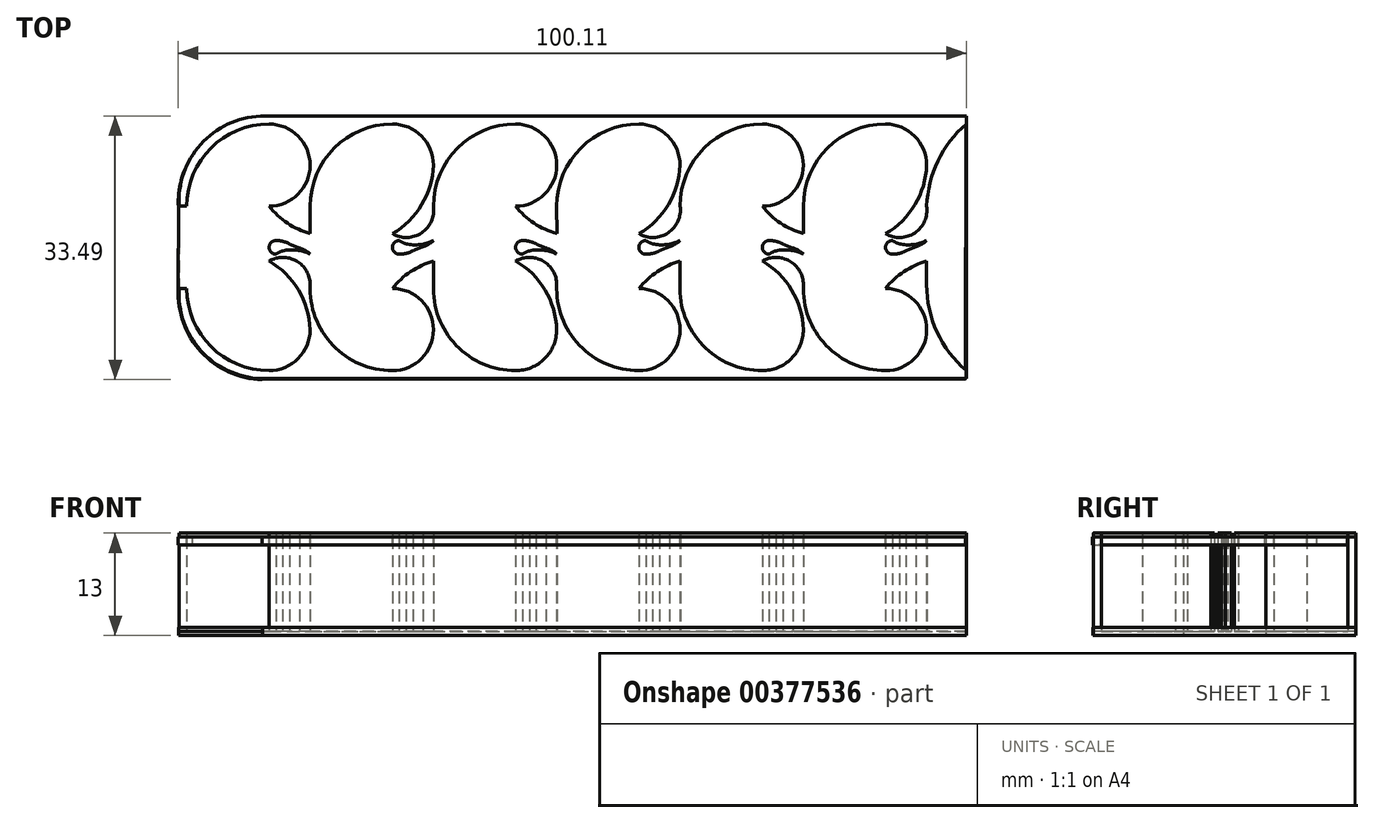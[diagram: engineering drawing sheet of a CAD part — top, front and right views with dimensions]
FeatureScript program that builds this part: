
annotation { "Feature Type Name" : "Feature", "Feature Type Description" : "" }
export const myFeature = defineFeature(function(context is Context, id is Id, definition is map)
    precondition{}
    {
        {
            var Q0;
            Q0=qCreatedBy(makeId("Top.planeOp"),FACE);
            var sketch = newSketch(context, id + "F0", { "sketchPlane" : qUnion([Q0])});
            skPoint(sketch, "E0", {"position": v(94.94, 29.27) * mm});
            skPoint(sketch, "E1", {"position": v(95.94, 28.27) * mm});
            skPoint(sketch, "E2", {"position": v(95.94, -3.06) * mm});
            skPoint(sketch, "E3", {"position": v(94.94, -4.06) * mm});
            skPoint(sketch, "E4", {"position": v(94.94, -3.06) * mm});
            skPoint(sketch, "E5", {"position": v(-3.06, 17.83) * mm});
            skPoint(sketch, "E6", {"position": v(-3.06, 7.38) * mm});
            skLineSegment(sketch, "E7", {"start": v(-3.06, 17.83) * mm, "end": v(-4.06, 17.83) * mm});
            skLineSegment(sketch, "E8", {"start": v(-4.06, 7.38) * mm, "end": v(-3.06, 7.38) * mm});
            skPoint(sketch, "E9", {"position": v(7.38, 28.27) * mm});
            skPoint(sketch, "E10", {"position": v(7.38, -3.06) * mm});
            skArc(sketch, "E11", {"start": v(7.38, 28.27) * mm, "mid": v(0, 25.21) * mm, "end": v(-3.06, 17.83) * mm});
            skArc(sketch, "E12", {"start": v(-3.06, 7.38) * mm, "mid": v(0, 0) * mm, "end": v(7.38, -3.06) * mm});
            skArc(sketch, "E13", {"start": v(7.38, 17.83) * mm, "mid": v(12.6, 23.05) * mm, "end": v(7.38, 28.27) * mm});
            skPoint(sketch, "E14", {"position": v(12.6, 23.05) * mm});
            skPoint(sketch, "E15", {"position": v(0, 25.21) * mm});
            skPoint(sketch, "E16", {"position": v(0, 0) * mm});
            skPoint(sketch, "E17", {"position": v(12.6, 2.16) * mm});
            skPoint(sketch, "E18", {"position": v(-4.06, 12.6) * mm});
            skPoint(sketch, "E19", {"position": v(7.38, 12.6) * mm});
            skPoint(sketch, "E20", {"position": v(7.38, 10.87) * mm});
            skPoint(sketch, "E21", {"position": v(7.38, 14.35) * mm});
            skArc(sketch, "E22", {"start": v(12.6, 2.16) * mm, "mid": v(11.12, 7.2) * mm, "end": v(7.38, 10.87) * mm});
            skArc(sketch, "E23", {"start": v(23.05, 28.27) * mm, "mid": v(15.66, 25.21) * mm, "end": v(12.6, 17.83) * mm});
            skArc(sketch, "E24", {"start": v(12.6, 7.86) * mm, "mid": v(15.49, 0.17) * mm, "end": v(23.03, -3.06) * mm});
            skPoint(sketch, "E25", {"position": v(28.27, 23.05) * mm});
            skPoint(sketch, "E26", {"position": v(15.66, 25.21) * mm});
            skPoint(sketch, "E27", {"position": v(15.49, 0.17) * mm});
            skPoint(sketch, "E28", {"position": v(28.27, 2.16) * mm});
            skPoint(sketch, "E29", {"position": v(23.05, 12.6) * mm});
            skPoint(sketch, "E30", {"position": v(23.05, 14.35) * mm});
            skArc(sketch, "E31", {"start": v(23.05, 14.35) * mm, "mid": v(26.78, 18.02) * mm, "end": v(28.27, 23.05) * mm});
            skPoint(sketch, "E32", {"position": v(11.12, 7.2) * mm});
            skLineSegment(sketch, "E33", {"start": v(12.6, 17.83) * mm, "end": v(12.6, 14.35) * mm});
            skArc(sketch, "E34", {"start": v(12.6, 7.86) * mm, "mid": v(10.86, 10.87) * mm, "end": v(7.38, 10.87) * mm});
            skArc(sketch, "E35", {"start": v(7.38, 17.83) * mm, "mid": v(9.73, 15.69) * mm, "end": v(12.6, 14.35) * mm});
            skPoint(sketch, "E36", {"position": v(12.6, 12.6) * mm});
            skPoint(sketch, "E37", {"position": v(7.38, 13.48) * mm});
            skPoint(sketch, "E38", {"position": v(12.6, 11.74) * mm});
            skPoint(sketch, "E39", {"position": v(12.6, 13.48) * mm});
            skPoint(sketch, "E40", {"position": v(9.12, 12.6) * mm});
            skPoint(sketch, "E41", {"position": v(10.87, 12.6) * mm});
            skLineSegment(sketch, "E42", {"start": v(7.38, 12.6) * mm, "end": v(9.12, 12.6) * mm});
            skLineSegment(sketch, "E43", {"start": v(9.12, 12.6) * mm, "end": v(10.87, 12.6) * mm});
            skPoint(sketch, "E44", {"position": v(8.25, 12.6) * mm});
            skPoint(sketch, "E45", {"position": v(10, 12.6) * mm});
            skPoint(sketch, "E46", {"position": v(11.74, 12.6) * mm});
            skArc(sketch, "E47", {"start": v(8.25, 13.48) * mm, "mid": v(7.38, 12.6) * mm, "end": v(8.25, 11.74) * mm});
            skArc(sketch, "E48", {"start": v(10, 13.04) * mm, "mid": v(9.15, 13.37) * mm, "end": v(8.25, 13.48) * mm});
            skPoint(sketch, "E49", {"position": v(12.6, 12.17) * mm});
            skPoint(sketch, "E50", {"position": v(12.6, 13.04) * mm});
            skPoint(sketch, "E51", {"position": v(10, 12.17) * mm});
            skArc(sketch, "E52", {"start": v(9.12, 12.17) * mm, "mid": v(8.67, 11.99) * mm, "end": v(8.25, 11.74) * mm});
            skPoint(sketch, "E53.endSnap0", {"position": v(8.25, 13.04) * mm});
            skPoint(sketch, "E54", {"position": v(11.27, 12.52) * mm});
            skPoint(sketch, "E55", {"position": v(11.27, 12.7) * mm});
            skArc(sketch, "E56", {"start": v(12.6, 11.74) * mm, "mid": v(11.98, 12.2) * mm, "end": v(11.27, 12.52) * mm});
            skArc(sketch, "E57", {"start": v(10, 13.04) * mm, "mid": v(10.62, 12.76) * mm, "end": v(11.27, 12.52) * mm});
            skArc(sketch, "E58", {"start": v(12.6, 11.74) * mm, "mid": v(10.9, 12.26) * mm, "end": v(9.12, 12.17) * mm});
            skArc(sketch, "E59", {"start": v(23.05, -3.06) * mm, "mid": v(28.27, 2.16) * mm, "end": v(23.05, 7.38) * mm});
            skArc(sketch, "E60", {"start": v(38.7, 28.27) * mm, "mid": v(31.33, 25.21) * mm, "end": v(28.27, 17.83) * mm});
            skArc(sketch, "E61", {"start": v(28.27, 7.86) * mm, "mid": v(31.15, 0.17) * mm, "end": v(38.7, -3.06) * mm});
            skArc(sketch, "E62", {"start": v(38.7, 17.83) * mm, "mid": v(43.93, 23.05) * mm, "end": v(38.7, 28.27) * mm});
            skPoint(sketch, "E63", {"position": v(43.93, 23.05) * mm});
            skPoint(sketch, "E64", {"position": v(31.33, 25.21) * mm});
            skPoint(sketch, "E65", {"position": v(31.15, 0.17) * mm});
            skPoint(sketch, "E66", {"position": v(43.93, 2.16) * mm});
            skPoint(sketch, "E67", {"position": v(38.7, 12.6) * mm});
            skPoint(sketch, "E68", {"position": v(38.7, 10.87) * mm});
            skPoint(sketch, "E69", {"position": v(38.7, 14.35) * mm});
            skArc(sketch, "E70", {"start": v(43.93, 2.16) * mm, "mid": v(42.45, 7.2) * mm, "end": v(38.7, 10.87) * mm});
            skArc(sketch, "E71", {"start": v(23.05, 14.35) * mm, "mid": v(26.76, 14.44) * mm, "end": v(28.27, 17.83) * mm});
            skPoint(sketch, "E72", {"position": v(26.78, 7.2) * mm});
            skArc(sketch, "E73", {"start": v(28.27, 10.87) * mm, "mid": v(25.39, 9.53) * mm, "end": v(23.05, 7.38) * mm});
            skLineSegment(sketch, "E74", {"start": v(28.27, 7.86) * mm, "end": v(28.27, 10.87) * mm});
            skPoint(sketch, "E75", {"position": v(28.27, 12.6) * mm});
            skPoint(sketch, "E76", {"position": v(23.05, 13.48) * mm});
            skPoint(sketch, "E77", {"position": v(28.27, 11.74) * mm});
            skPoint(sketch, "E78", {"position": v(28.27, 13.48) * mm});
            skPoint(sketch, "E79", {"position": v(24.79, 12.6) * mm});
            skPoint(sketch, "E80", {"position": v(26.53, 12.6) * mm});
            skLineSegment(sketch, "E81", {"start": v(23.05, 12.6) * mm, "end": v(24.79, 12.6) * mm});
            skLineSegment(sketch, "E82", {"start": v(24.79, 12.6) * mm, "end": v(26.53, 12.6) * mm});
            skPoint(sketch, "E83", {"position": v(23.92, 12.6) * mm});
            skPoint(sketch, "E84", {"position": v(25.66, 12.6) * mm});
            skPoint(sketch, "E85", {"position": v(27.4, 12.6) * mm});
            skArc(sketch, "E86", {"start": v(23.92, 13.48) * mm, "mid": v(23.05, 12.6) * mm, "end": v(23.92, 11.74) * mm});
            skPoint(sketch, "E87", {"position": v(28.27, 12.17) * mm});
            skPoint(sketch, "E88", {"position": v(28.27, 13.04) * mm});
            skPoint(sketch, "E89", {"position": v(25.66, 12.17) * mm});
            skArc(sketch, "E90", {"start": v(23.92, 13.48) * mm, "mid": v(24.34, 13.23) * mm, "end": v(24.79, 13.04) * mm});
            skPoint(sketch, "E90.endSnap0", {"position": v(23.92, 13.04) * mm});
            skArc(sketch, "E91", {"start": v(23.92, 11.74) * mm, "mid": v(24.82, 11.84) * mm, "end": v(25.66, 12.17) * mm});
            skPoint(sketch, "E92", {"position": v(26.93, 12.52) * mm});
            skPoint(sketch, "E93", {"position": v(26.93, 12.7) * mm});
            skArc(sketch, "E94", {"start": v(26.93, 12.7) * mm, "mid": v(26.29, 12.45) * mm, "end": v(25.66, 12.17) * mm});
            skArc(sketch, "E95", {"start": v(26.93, 12.7) * mm, "mid": v(27.65, 13.01) * mm, "end": v(28.27, 13.48) * mm});
            skArc(sketch, "E96", {"start": v(24.79, 13.04) * mm, "mid": v(26.57, 12.96) * mm, "end": v(28.27, 13.48) * mm});
            skArc(sketch, "E97", {"start": v(54.37, 28.27) * mm, "mid": v(46.99, 25.21) * mm, "end": v(43.93, 17.83) * mm});
            skArc(sketch, "E98", {"start": v(43.93, 7.86) * mm, "mid": v(46.81, 0.17) * mm, "end": v(54.36, -3.06) * mm});
            skPoint(sketch, "E99", {"position": v(59.6, 23.05) * mm});
            skPoint(sketch, "E100", {"position": v(46.99, 25.21) * mm});
            skPoint(sketch, "E101", {"position": v(46.81, 0.17) * mm});
            skPoint(sketch, "E102", {"position": v(59.6, 2.16) * mm});
            skPoint(sketch, "E103", {"position": v(54.37, 12.6) * mm});
            skPoint(sketch, "E104", {"position": v(54.37, 14.35) * mm});
            skArc(sketch, "E105", {"start": v(54.37, 14.35) * mm, "mid": v(58.1, 18.02) * mm, "end": v(59.6, 23.05) * mm});
            skPoint(sketch, "E106", {"position": v(42.45, 7.2) * mm});
            skLineSegment(sketch, "E107", {"start": v(43.93, 17.83) * mm, "end": v(43.93, 14.35) * mm});
            skArc(sketch, "E108", {"start": v(43.93, 7.86) * mm, "mid": v(42.19, 10.87) * mm, "end": v(38.7, 10.87) * mm});
            skArc(sketch, "E109", {"start": v(38.7, 17.83) * mm, "mid": v(41.05, 15.69) * mm, "end": v(43.93, 14.35) * mm});
            skPoint(sketch, "E110", {"position": v(43.93, 12.6) * mm});
            skPoint(sketch, "E111", {"position": v(38.7, 13.48) * mm});
            skPoint(sketch, "E112", {"position": v(38.7, 11.74) * mm});
            skPoint(sketch, "E113", {"position": v(43.93, 11.74) * mm});
            skPoint(sketch, "E114", {"position": v(43.93, 13.48) * mm});
            skPoint(sketch, "E115", {"position": v(40.45, 12.6) * mm});
            skPoint(sketch, "E116", {"position": v(42.2, 12.6) * mm});
            skLineSegment(sketch, "E117", {"start": v(38.7, 12.6) * mm, "end": v(40.45, 12.6) * mm});
            skLineSegment(sketch, "E118", {"start": v(40.45, 12.6) * mm, "end": v(42.2, 12.6) * mm});
            skPoint(sketch, "E119", {"position": v(39.58, 12.6) * mm});
            skPoint(sketch, "E120", {"position": v(41.32, 12.6) * mm});
            skPoint(sketch, "E121", {"position": v(43.06, 12.6) * mm});
            skArc(sketch, "E122", {"start": v(39.58, 13.48) * mm, "mid": v(38.7, 12.6) * mm, "end": v(39.58, 11.74) * mm});
            skArc(sketch, "E123", {"start": v(41.32, 13.04) * mm, "mid": v(40.48, 13.37) * mm, "end": v(39.58, 13.48) * mm});
            skPoint(sketch, "E124", {"position": v(43.93, 12.17) * mm});
            skPoint(sketch, "E125", {"position": v(43.93, 13.04) * mm});
            skPoint(sketch, "E126", {"position": v(41.32, 12.17) * mm});
            skArc(sketch, "E127", {"start": v(40.45, 12.17) * mm, "mid": v(40, 11.99) * mm, "end": v(39.58, 11.74) * mm});
            skPoint(sketch, "E128.endSnap0", {"position": v(39.58, 13.04) * mm});
            skPoint(sketch, "E129", {"position": v(42.6, 12.52) * mm});
            skPoint(sketch, "E130", {"position": v(42.6, 12.7) * mm});
            skArc(sketch, "E131", {"start": v(43.93, 11.74) * mm, "mid": v(43.3, 12.2) * mm, "end": v(42.6, 12.52) * mm});
            skArc(sketch, "E132", {"start": v(41.32, 13.04) * mm, "mid": v(41.95, 12.76) * mm, "end": v(42.6, 12.52) * mm});
            skArc(sketch, "E133", {"start": v(43.93, 11.74) * mm, "mid": v(42.23, 12.26) * mm, "end": v(40.45, 12.17) * mm});
            skArc(sketch, "E134", {"start": v(54.37, -3.06) * mm, "mid": v(59.6, 2.16) * mm, "end": v(54.37, 7.38) * mm});
            skArc(sketch, "E135", {"start": v(70.03, 28.27) * mm, "mid": v(62.65, 25.21) * mm, "end": v(59.6, 17.83) * mm});
            skArc(sketch, "E136", {"start": v(59.6, 7.86) * mm, "mid": v(62.48, 0.17) * mm, "end": v(70.02, -3.06) * mm});
            skArc(sketch, "E137", {"start": v(70.03, 17.83) * mm, "mid": v(75.25, 23.05) * mm, "end": v(70.03, 28.27) * mm});
            skPoint(sketch, "E138", {"position": v(75.25, 23.05) * mm});
            skPoint(sketch, "E139", {"position": v(62.65, 25.21) * mm});
            skPoint(sketch, "E140", {"position": v(62.48, 0.17) * mm});
            skPoint(sketch, "E141", {"position": v(75.25, 2.16) * mm});
            skPoint(sketch, "E142", {"position": v(70.03, 12.6) * mm});
            skPoint(sketch, "E143", {"position": v(70.03, 10.87) * mm});
            skArc(sketch, "E144", {"start": v(75.25, 2.16) * mm, "mid": v(73.77, 7.2) * mm, "end": v(70.03, 10.87) * mm});
            skArc(sketch, "E145", {"start": v(54.37, 14.35) * mm, "mid": v(58.08, 14.44) * mm, "end": v(59.6, 17.83) * mm});
            skPoint(sketch, "E146", {"position": v(58.1, 7.2) * mm});
            skArc(sketch, "E147", {"start": v(59.6, 10.87) * mm, "mid": v(56.71, 9.53) * mm, "end": v(54.37, 7.38) * mm});
            skLineSegment(sketch, "E148", {"start": v(59.6, 7.86) * mm, "end": v(59.6, 10.87) * mm});
            skPoint(sketch, "E149", {"position": v(59.6, 12.6) * mm});
            skPoint(sketch, "E150", {"position": v(54.37, 13.48) * mm});
            skPoint(sketch, "E151", {"position": v(59.6, 11.74) * mm});
            skPoint(sketch, "E152", {"position": v(59.6, 13.48) * mm});
            skPoint(sketch, "E153", {"position": v(56.11, 12.6) * mm});
            skPoint(sketch, "E154", {"position": v(57.85, 12.6) * mm});
            skLineSegment(sketch, "E155", {"start": v(54.37, 12.6) * mm, "end": v(56.11, 12.6) * mm});
            skLineSegment(sketch, "E156", {"start": v(56.11, 12.6) * mm, "end": v(57.85, 12.6) * mm});
            skPoint(sketch, "E157", {"position": v(55.24, 12.6) * mm});
            skPoint(sketch, "E158", {"position": v(56.98, 12.6) * mm});
            skPoint(sketch, "E159", {"position": v(58.72, 12.6) * mm});
            skArc(sketch, "E160", {"start": v(55.24, 13.48) * mm, "mid": v(54.37, 12.6) * mm, "end": v(55.24, 11.74) * mm});
            skPoint(sketch, "E161", {"position": v(59.6, 12.17) * mm});
            skPoint(sketch, "E162", {"position": v(59.6, 13.04) * mm});
            skPoint(sketch, "E163", {"position": v(56.98, 12.17) * mm});
            skArc(sketch, "E164", {"start": v(55.24, 13.48) * mm, "mid": v(55.66, 13.23) * mm, "end": v(56.11, 13.04) * mm});
            skPoint(sketch, "E164.endSnap0", {"position": v(55.24, 13.04) * mm});
            skArc(sketch, "E165", {"start": v(55.24, 11.74) * mm, "mid": v(56.14, 11.84) * mm, "end": v(56.98, 12.17) * mm});
            skPoint(sketch, "E166", {"position": v(58.26, 12.7) * mm});
            skArc(sketch, "E167", {"start": v(58.26, 12.7) * mm, "mid": v(57.61, 12.45) * mm, "end": v(56.98, 12.17) * mm});
            skArc(sketch, "E168", {"start": v(58.26, 12.7) * mm, "mid": v(58.97, 13.01) * mm, "end": v(59.6, 13.48) * mm});
            skArc(sketch, "E169", {"start": v(56.11, 13.04) * mm, "mid": v(57.9, 12.96) * mm, "end": v(59.6, 13.48) * mm});
            skPoint(sketch, "E170", {"position": v(70.03, 14.35) * mm});
            skArc(sketch, "E171", {"start": v(85.7, 28.27) * mm, "mid": v(78.31, 25.21) * mm, "end": v(75.26, 17.83) * mm});
            skArc(sketch, "E172", {"start": v(75.26, 7.86) * mm, "mid": v(78.14, 0.17) * mm, "end": v(85.69, -3.06) * mm});
            skPoint(sketch, "E173", {"position": v(90.92, 23.05) * mm});
            skPoint(sketch, "E174", {"position": v(78.31, 25.21) * mm});
            skPoint(sketch, "E175", {"position": v(78.14, 0.17) * mm});
            skPoint(sketch, "E176", {"position": v(90.92, 2.16) * mm});
            skPoint(sketch, "E177", {"position": v(85.7, 12.6) * mm});
            skPoint(sketch, "E178", {"position": v(85.7, 10.87) * mm});
            skPoint(sketch, "E179", {"position": v(85.7, 14.35) * mm});
            skArc(sketch, "E180", {"start": v(85.7, 14.35) * mm, "mid": v(89.43, 18.02) * mm, "end": v(90.92, 23.05) * mm});
            skPoint(sketch, "E181", {"position": v(73.77, 7.2) * mm});
            skLineSegment(sketch, "E182", {"start": v(75.26, 17.83) * mm, "end": v(75.26, 14.35) * mm});
            skArc(sketch, "E183", {"start": v(75.26, 7.86) * mm, "mid": v(73.52, 10.87) * mm, "end": v(70.03, 10.87) * mm});
            skArc(sketch, "E184", {"start": v(70.03, 17.83) * mm, "mid": v(72.38, 15.69) * mm, "end": v(75.26, 14.35) * mm});
            skPoint(sketch, "E185", {"position": v(75.26, 12.6) * mm});
            skPoint(sketch, "E186", {"position": v(75.26, 11.74) * mm});
            skPoint(sketch, "E187", {"position": v(75.26, 13.48) * mm});
            skPoint(sketch, "E188", {"position": v(71.77, 12.6) * mm});
            skPoint(sketch, "E189", {"position": v(73.52, 12.6) * mm});
            skLineSegment(sketch, "E190", {"start": v(70.03, 12.6) * mm, "end": v(71.77, 12.6) * mm});
            skLineSegment(sketch, "E191", {"start": v(71.77, 12.6) * mm, "end": v(73.52, 12.6) * mm});
            skPoint(sketch, "E192", {"position": v(70.9, 12.6) * mm});
            skPoint(sketch, "E193", {"position": v(72.65, 12.6) * mm});
            skPoint(sketch, "E194", {"position": v(74.39, 12.6) * mm});
            skArc(sketch, "E195", {"start": v(70.9, 13.48) * mm, "mid": v(70.03, 12.6) * mm, "end": v(70.9, 11.74) * mm});
            skArc(sketch, "E196", {"start": v(72.65, 13.04) * mm, "mid": v(71.8, 13.37) * mm, "end": v(70.9, 13.48) * mm});
            skPoint(sketch, "E197", {"position": v(75.26, 12.17) * mm});
            skPoint(sketch, "E198", {"position": v(75.26, 13.04) * mm});
            skPoint(sketch, "E199", {"position": v(72.65, 12.17) * mm});
            skArc(sketch, "E200", {"start": v(71.77, 12.17) * mm, "mid": v(71.32, 11.99) * mm, "end": v(70.9, 11.74) * mm});
            skPoint(sketch, "E201.endSnap0", {"position": v(70.9, 13.04) * mm});
            skPoint(sketch, "E202", {"position": v(73.92, 12.52) * mm});
            skPoint(sketch, "E203", {"position": v(73.92, 12.7) * mm});
            skArc(sketch, "E204", {"start": v(75.26, 11.74) * mm, "mid": v(74.63, 12.2) * mm, "end": v(73.92, 12.52) * mm});
            skArc(sketch, "E205", {"start": v(72.65, 13.04) * mm, "mid": v(73.27, 12.76) * mm, "end": v(73.92, 12.52) * mm});
            skArc(sketch, "E206", {"start": v(75.26, 11.74) * mm, "mid": v(73.55, 12.26) * mm, "end": v(71.77, 12.17) * mm});
            skArc(sketch, "E207", {"start": v(85.7, -3.06) * mm, "mid": v(90.92, 2.16) * mm, "end": v(85.7, 7.38) * mm});
            skPoint(sketch, "E208", {"position": v(93.98, 25.21) * mm});
            skPoint(sketch, "E209", {"position": v(93.8, 0.17) * mm});
            skArc(sketch, "E210", {"start": v(85.7, 14.35) * mm, "mid": v(89.4, 14.44) * mm, "end": v(90.92, 17.83) * mm});
            skPoint(sketch, "E211", {"position": v(89.43, 7.2) * mm});
            skArc(sketch, "E212", {"start": v(90.92, 10.87) * mm, "mid": v(88.04, 9.53) * mm, "end": v(85.7, 7.38) * mm});
            skLineSegment(sketch, "E213", {"start": v(90.92, 7.86) * mm, "end": v(90.92, 10.87) * mm});
            skPoint(sketch, "E214", {"position": v(90.92, 12.6) * mm});
            skPoint(sketch, "E215", {"position": v(90.92, 11.74) * mm});
            skPoint(sketch, "E216", {"position": v(90.92, 13.48) * mm});
            skPoint(sketch, "E217", {"position": v(87.44, 12.6) * mm});
            skPoint(sketch, "E218", {"position": v(89.18, 12.6) * mm});
            skLineSegment(sketch, "E219", {"start": v(85.7, 12.6) * mm, "end": v(87.44, 12.6) * mm});
            skLineSegment(sketch, "E220", {"start": v(87.44, 12.6) * mm, "end": v(89.18, 12.6) * mm});
            skPoint(sketch, "E221", {"position": v(86.57, 12.6) * mm});
            skPoint(sketch, "E222", {"position": v(88.3, 12.6) * mm});
            skPoint(sketch, "E223", {"position": v(90.05, 12.6) * mm});
            skArc(sketch, "E224", {"start": v(86.57, 13.48) * mm, "mid": v(85.7, 12.6) * mm, "end": v(86.57, 11.74) * mm});
            skPoint(sketch, "E225", {"position": v(90.92, 12.17) * mm});
            skPoint(sketch, "E226", {"position": v(90.92, 13.04) * mm});
            skPoint(sketch, "E227", {"position": v(88.3, 12.17) * mm});
            skArc(sketch, "E228", {"start": v(86.57, 13.48) * mm, "mid": v(86.99, 13.23) * mm, "end": v(87.44, 13.04) * mm});
            skPoint(sketch, "E228.endSnap0", {"position": v(86.57, 13.04) * mm});
            skArc(sketch, "E229", {"start": v(86.57, 11.74) * mm, "mid": v(87.47, 11.84) * mm, "end": v(88.3, 12.17) * mm});
            skPoint(sketch, "E230", {"position": v(89.58, 12.52) * mm});
            skPoint(sketch, "E231", {"position": v(89.58, 12.7) * mm});
            skArc(sketch, "E232", {"start": v(89.58, 12.7) * mm, "mid": v(88.94, 12.45) * mm, "end": v(88.3, 12.17) * mm});
            skArc(sketch, "E233", {"start": v(89.58, 12.7) * mm, "mid": v(90.3, 13.01) * mm, "end": v(90.92, 13.48) * mm});
            skArc(sketch, "E234", {"start": v(87.44, 13.04) * mm, "mid": v(89.22, 12.96) * mm, "end": v(90.92, 13.48) * mm});
            skArc(sketch, "E235", {"start": v(23.05, -3.06) * mm, "mid": v(26.74, -1.53) * mm, "end": v(28.27, 2.16) * mm});
            skArc(sketch, "E236", {"start": v(7.38, -3.06) * mm, "mid": v(11.07, -1.53) * mm, "end": v(12.6, 2.16) * mm});
            skArc(sketch, "E237", {"start": v(28.27, 23.05) * mm, "mid": v(26.74, 26.74) * mm, "end": v(23.05, 28.27) * mm});
            skArc(sketch, "E238", {"start": v(38.7, -3.06) * mm, "mid": v(42.4, -1.53) * mm, "end": v(43.93, 2.16) * mm});
            skArc(sketch, "E239", {"start": v(70.02, -3.06) * mm, "mid": v(73.72, -1.53) * mm, "end": v(75.25, 2.16) * mm});
            skArc(sketch, "E240", {"start": v(59.6, 23.05) * mm, "mid": v(58.06, 26.74) * mm, "end": v(54.37, 28.27) * mm});
            skArc(sketch, "E241", {"start": v(90.92, 23.05) * mm, "mid": v(89.39, 26.74) * mm, "end": v(85.7, 28.27) * mm});
            skArc(sketch, "E242", {"start": v(90.92, 7.86) * mm, "mid": v(92.24, 1.85) * mm, "end": v(95.94, -3.06) * mm});
            skArc(sketch, "E243", {"start": v(95.94, 28.27) * mm, "mid": v(92.34, 23.58) * mm, "end": v(90.92, 17.83) * mm});
            skPoint(sketch, "E244", {"position": v(7.38, 29.27) * mm});
            skPoint(sketch, "E245", {"position": v(7.38, -4.06) * mm});
            skPoint(sketch, "E246", {"position": v(-4.06, 6.38) * mm});
            skPoint(sketch, "E247", {"position": v(-4.06, 18.83) * mm});
            skArc(sketch, "E248", {"start": v(-4.06, 6.38) * mm, "mid": v(-0.53, -1.24) * mm, "end": v(7.38, -4.06) * mm});
            skArc(sketch, "E249", {"start": v(7.38, 29.27) * mm, "mid": v(-0.53, 26.46) * mm, "end": v(-4.06, 18.83) * mm});
            skLineSegment(sketch, "E250", {"start": v(7.38, 29.27) * mm, "end": v(95.94, 29.27) * mm});
            skLineSegment(sketch, "E251", {"start": v(95.94, 29.27) * mm, "end": v(95.94, 28.27) * mm});
            skLineSegment(sketch, "E252", {"start": v(95.94, -3.06) * mm, "end": v(95.94, -4.06) * mm});
            skLineSegment(sketch, "E253", {"start": v(95.94, -4.06) * mm, "end": v(7.38, -4.06) * mm});
            skLineSegment(sketch, "E254", {"start": v(-4.06, 6.38) * mm, "end": v(-4.06, 7.38) * mm});
            skLineSegment(sketch, "E255", {"start": v(-3.06, 7.38) * mm, "end": v(-4.06, 7.38) * mm});
            skLineSegment(sketch, "E256", {"start": v(-4.06, 17.83) * mm, "end": v(-3.06, 17.83) * mm});
            skLineSegment(sketch, "E257", {"start": v(-4.06, 17.83) * mm, "end": v(-4.06, 18.83) * mm});
            skPoint(sketch, "E258", {"position": v(11.07, -1.53) * mm});
            skPoint(sketch, "E259", {"position": v(26.74, -1.53) * mm});
            skPoint(sketch, "E260", {"position": v(42.4, -1.53) * mm});
            skPoint(sketch, "E261", {"position": v(73.72, -1.53) * mm});
            skPoint(sketch, "E262", {"position": v(10.86, 10.87) * mm});
            skPoint(sketch, "E263", {"position": v(25.39, 9.53) * mm});
            skPoint(sketch, "E264", {"position": v(42.19, 10.87) * mm});
            skPoint(sketch, "E265", {"position": v(56.71, 9.53) * mm});
            skPoint(sketch, "E266", {"position": v(73.52, 10.87) * mm});
            skPoint(sketch, "E267", {"position": v(88.04, 9.53) * mm});
            skArc(sketch, "E268", {"start": v(12.6, 7.86) * mm, "mid": v(15.5, 0.17) * mm, "end": v(23.05, -3.06) * mm});
            skArc(sketch, "E269", {"start": v(28.27, 2.16) * mm, "mid": v(26.74, 5.85) * mm, "end": v(23.05, 7.38) * mm});
            skLineSegment(sketch, "E270", {"start": v(28.27, 10.87) * mm, "end": v(28.27, 7.86) * mm});
            skArc(sketch, "E271", {"start": v(43.93, 7.86) * mm, "mid": v(46.82, 0.17) * mm, "end": v(54.37, -3.06) * mm});
            skLineSegment(sketch, "E272", {"start": v(59.6, 10.87) * mm, "end": v(59.6, 7.86) * mm});
            skArc(sketch, "E273", {"start": v(75.26, 7.86) * mm, "mid": v(78.14, 0.17) * mm, "end": v(85.7, -3.06) * mm});
            skSolve(sketch);
        }
        {
            var Q0;
            Q0=makeQuery(id+"F0.imprint","IMPRINT",FACE,{"disambiguationData":[TD([[makeQuery(id+"F0.imprint","IMPRINT",EDGE,{"derivedFrom":sQuery(id+"F0.wireOp",EDGE,"E11")}),-1.0]])]});
            var Q1;
            {var subQ8=sQuery(id+"F0.wireOp",EDGE,"E207");Q1=makeQuery(id+"F0.imprint","IMPRINT",FACE,{"disambiguationData":[TD([[makeQuery(id+"F0.imprint","IMPRINT",EDGE,{"derivedFrom":subQ8}),-1.0]])]});}
            var Q2;
            {var subQ1=sQuery(id+"F0.wireOp",EDGE,"E48");Q2=makeQuery(id+"F0.imprint","IMPRINT",FACE,{"disambiguationData":[TD([[makeQuery(id+"F0.imprint","IMPRINT",EDGE,{"derivedFrom":subQ1}),1.0]])]});}
            var Q3;
            {var subQ1=sQuery(id+"F0.wireOp",EDGE,"E90");Q3=makeQuery(id+"F0.imprint","IMPRINT",FACE,{"disambiguationData":[TD([[makeQuery(id+"F0.imprint","IMPRINT",EDGE,{"derivedFrom":subQ1}),-1.0]])]});}
            var Q4;
            {var subQ1=sQuery(id+"F0.wireOp",EDGE,"E123");Q4=makeQuery(id+"F0.imprint","IMPRINT",FACE,{"disambiguationData":[TD([[makeQuery(id+"F0.imprint","IMPRINT",EDGE,{"derivedFrom":subQ1}),1.0]])]});}
            var Q5;
            {var subQ1=sQuery(id+"F0.wireOp",EDGE,"E164");Q5=makeQuery(id+"F0.imprint","IMPRINT",FACE,{"disambiguationData":[TD([[makeQuery(id+"F0.imprint","IMPRINT",EDGE,{"derivedFrom":subQ1}),-1.0]])]});}
            var Q6;
            {var subQ1=sQuery(id+"F0.wireOp",EDGE,"E196");Q6=makeQuery(id+"F0.imprint","IMPRINT",FACE,{"disambiguationData":[TD([[makeQuery(id+"F0.imprint","IMPRINT",EDGE,{"derivedFrom":subQ1}),1.0]])]});}
            var Q7;
            {var subQ1=sQuery(id+"F0.wireOp",EDGE,"E228");Q7=makeQuery(id+"F0.imprint","IMPRINT",FACE,{"disambiguationData":[TD([[makeQuery(id+"F0.imprint","IMPRINT",EDGE,{"derivedFrom":subQ1}),-1.0]])]});}
            extrude(context, id + "F1", {"entities" : qUnion([Q0, Q1, Q2, Q3, Q4, Q5, Q6, Q7]), "depth" : 12 * mm});
        }
        {
            var Q0;
            Q0=qCreatedBy(makeId("Top.planeOp"),FACE);
            var sketch = newSketch(context, id + "F2", { "sketchPlane" : qUnion([Q0])});
            skPoint(sketch, "E274", {"position": v(-4.05, 17.83) * mm});
            skPoint(sketch, "E275", {"position": v(-4.06, 7.39) * mm});
            skPoint(sketch, "E276", {"position": v(6.57, 29.28) * mm});
            skPoint(sketch, "E277", {"position": v(6.57, -4.11) * mm});
            skPoint(sketch, "E278", {"position": v(95.96, 29.28) * mm});
            skPoint(sketch, "E279", {"position": v(95.95, -4.06) * mm});
            skLineSegment(sketch, "E280", {"start": v(6.57, 29.28) * mm, "end": v(95.96, 29.28) * mm});
            skLineSegment(sketch, "E281", {"start": v(95.95, -4.06) * mm, "end": v(95.96, 29.28) * mm});
            skLineSegment(sketch, "E282", {"start": v(95.95, -4.06) * mm, "end": v(6.57, -4.11) * mm});
            skLineSegment(sketch, "E283", {"start": v(-4.05, 17.83) * mm, "end": v(-4.06, 7.39) * mm});
            skArc(sketch, "E284", {"start": v(6.57, 29.28) * mm, "mid": v(-1.17, 25.8) * mm, "end": v(-4.05, 17.83) * mm});
            skArc(sketch, "E285", {"start": v(-4.06, 7.39) * mm, "mid": v(-1.16, -0.6) * mm, "end": v(6.57, -4.11) * mm});
            skSolve(sketch);
        }
        {
            var Q0;
            Q0=makeQuery(id+"F2.imprint","IMPRINT",FACE,{"disambiguationData":[TD([[makeQuery(id+"F2.imprint","IMPRINT",EDGE,{"derivedFrom":sQuery(id+"F2.wireOp",EDGE,"E280")}),-1.0]])]});
            extrude(context, id + "F3", {"entities" : qUnion([Q0]), "endBound" : BoundingType.SYMMETRIC, "depth" : 1 * mm});
        }
        {
            var Q0;
            Q0=makeQuery(id+"F1.opExtrude","CAP_FACE",FACE,{"disambiguationData":[OSD([sQuery(id+"F0.wireOp",EDGE,"E11"),sQuery(id+"F0.wireOp",EDGE,"E13"),sQuery(id+"F0.wireOp",EDGE,"E23"),sQuery(id+"F0.wireOp",EDGE,"E33"),sQuery(id+"F0.wireOp",EDGE,"E35"),sQuery(id+"F0.wireOp",EDGE,"E31"),sQuery(id+"F0.wireOp",EDGE,"E60"),sQuery(id+"F0.wireOp",EDGE,"E71"),sQuery(id+"F0.wireOp",EDGE,"E62"),sQuery(id+"F0.wireOp",EDGE,"E97"),sQuery(id+"F0.wireOp",EDGE,"E107"),sQuery(id+"F0.wireOp",EDGE,"E109"),sQuery(id+"F0.wireOp",EDGE,"E105"),sQuery(id+"F0.wireOp",EDGE,"E135"),sQuery(id+"F0.wireOp",EDGE,"E145"),sQuery(id+"F0.wireOp",EDGE,"E137"),sQuery(id+"F0.wireOp",EDGE,"E171"),sQuery(id+"F0.wireOp",EDGE,"E182"),sQuery(id+"F0.wireOp",EDGE,"E184"),sQuery(id+"F0.wireOp",EDGE,"E180"),sQuery(id+"F0.wireOp",EDGE,"E210"),sQuery(id+"F0.wireOp",EDGE,"E237"),sQuery(id+"F0.wireOp",EDGE,"E240"),sQuery(id+"F0.wireOp",EDGE,"E241"),sQuery(id+"F0.wireOp",EDGE,"E243"),sQuery(id+"F0.wireOp",EDGE,"E249"),sQuery(id+"F0.wireOp",EDGE,"E250"),sQuery(id+"F0.wireOp",EDGE,"E251"),sQuery(id+"F0.wireOp",EDGE,"E256"),sQuery(id+"F0.wireOp",EDGE,"E257")])],"isStart":false});
            var sketch = newSketch(context, id + "F4", { "sketchPlane" : qUnion([Q0])});
            skPoint(sketch, "E286", {"position": v(-4.13, 17.74) * mm});
            skPoint(sketch, "E287", {"position": v(-4.14, 7.3) * mm});
            skPoint(sketch, "E288", {"position": v(6.5, 29.2) * mm});
            skPoint(sketch, "E289", {"position": v(6.5, -4.2) * mm});
            skPoint(sketch, "E290", {"position": v(95.89, 29.2) * mm});
            skPoint(sketch, "E291", {"position": v(95.87, -4.14) * mm});
            skLineSegment(sketch, "E292", {"start": v(6.5, 29.2) * mm, "end": v(95.89, 29.2) * mm});
            skLineSegment(sketch, "E293", {"start": v(95.87, -4.14) * mm, "end": v(95.89, 29.2) * mm});
            skLineSegment(sketch, "E294", {"start": v(95.87, -4.14) * mm, "end": v(6.5, -4.2) * mm});
            skLineSegment(sketch, "E295", {"start": v(-4.13, 17.74) * mm, "end": v(-4.14, 7.3) * mm});
            skArc(sketch, "E296", {"start": v(6.5, 29.2) * mm, "mid": v(-1.24, 25.72) * mm, "end": v(-4.13, 17.74) * mm});
            skArc(sketch, "E297", {"start": v(-4.14, 7.3) * mm, "mid": v(-1.24, -0.69) * mm, "end": v(6.5, -4.2) * mm});
            skSolve(sketch);
        }
        {
            var Q0;
            {var subQ1=sQuery(id+"F4.wireOp",EDGE,"E294");Q0=makeQuery(id+"F4.imprint","IMPRINT",FACE,{"disambiguationData":[TD([[makeQuery(id+"F4.imprint","IMPRINT",EDGE,{"derivedFrom":subQ1}),-1.0]])]});}
            extrude(context, id + "F5", {"entities" : qUnion([Q0]), "depth" : -1 * mm});
        }
        {
            var Q0;
            Q0=makeQuery(id+"F1.opExtrude","CAP_FACE",FACE,{"disambiguationData":[OSD([sQuery(id+"F0.wireOp",EDGE,"E11"),sQuery(id+"F0.wireOp",EDGE,"E13"),sQuery(id+"F0.wireOp",EDGE,"E23"),sQuery(id+"F0.wireOp",EDGE,"E33"),sQuery(id+"F0.wireOp",EDGE,"E35"),sQuery(id+"F0.wireOp",EDGE,"E31"),sQuery(id+"F0.wireOp",EDGE,"E60"),sQuery(id+"F0.wireOp",EDGE,"E71"),sQuery(id+"F0.wireOp",EDGE,"E62"),sQuery(id+"F0.wireOp",EDGE,"E97"),sQuery(id+"F0.wireOp",EDGE,"E107"),sQuery(id+"F0.wireOp",EDGE,"E109"),sQuery(id+"F0.wireOp",EDGE,"E105"),sQuery(id+"F0.wireOp",EDGE,"E135"),sQuery(id+"F0.wireOp",EDGE,"E145"),sQuery(id+"F0.wireOp",EDGE,"E137"),sQuery(id+"F0.wireOp",EDGE,"E171"),sQuery(id+"F0.wireOp",EDGE,"E182"),sQuery(id+"F0.wireOp",EDGE,"E184"),sQuery(id+"F0.wireOp",EDGE,"E180"),sQuery(id+"F0.wireOp",EDGE,"E210"),sQuery(id+"F0.wireOp",EDGE,"E237"),sQuery(id+"F0.wireOp",EDGE,"E240"),sQuery(id+"F0.wireOp",EDGE,"E241"),sQuery(id+"F0.wireOp",EDGE,"E243"),sQuery(id+"F0.wireOp",EDGE,"E249"),sQuery(id+"F0.wireOp",EDGE,"E250"),sQuery(id+"F0.wireOp",EDGE,"E251"),sQuery(id+"F0.wireOp",EDGE,"E256"),sQuery(id+"F0.wireOp",EDGE,"E257")])],"isStart":false});
            extrude(context, id + "F6", {"entities" : qUnion([Q0]), "depth" : 0.5 * mm});
        }
        {
            var Q0;
            Q0=makeQuery(id+"F1.opExtrude","CAP_FACE",FACE,{"disambiguationData":[OSD([sQuery(id+"F0.wireOp",EDGE,"E224"),sQuery(id+"F0.wireOp",EDGE,"E228"),sQuery(id+"F0.wireOp",EDGE,"E229"),sQuery(id+"F0.wireOp",EDGE,"E232"),sQuery(id+"F0.wireOp",EDGE,"E233"),sQuery(id+"F0.wireOp",EDGE,"E234")])],"isStart":false});
            var Q1;
            Q1=makeQuery(id+"F1.opExtrude","CAP_FACE",FACE,{"disambiguationData":[OSD([sQuery(id+"F0.wireOp",EDGE,"E207"),sQuery(id+"F0.wireOp",EDGE,"E212"),sQuery(id+"F0.wireOp",EDGE,"E213"),sQuery(id+"F0.wireOp",EDGE,"E236"),sQuery(id+"F0.wireOp",EDGE,"E242"),sQuery(id+"F0.wireOp",EDGE,"E248"),sQuery(id+"F0.wireOp",EDGE,"E252"),sQuery(id+"F0.wireOp",EDGE,"E253"),sQuery(id+"F0.wireOp",EDGE,"E254"),sQuery(id+"F0.wireOp",EDGE,"E255"),sQuery(id+"F0.wireOp",EDGE,"E12"),sQuery(id+"F0.wireOp",EDGE,"E22"),sQuery(id+"F0.wireOp",EDGE,"E34"),sQuery(id+"F0.wireOp",EDGE,"E268"),sQuery(id+"F0.wireOp",EDGE,"E73"),sQuery(id+"F0.wireOp",EDGE,"E270"),sQuery(id+"F0.wireOp",EDGE,"E61"),sQuery(id+"F0.wireOp",EDGE,"E238"),sQuery(id+"F0.wireOp",EDGE,"E70"),sQuery(id+"F0.wireOp",EDGE,"E108"),sQuery(id+"F0.wireOp",EDGE,"E271"),sQuery(id+"F0.wireOp",EDGE,"E59"),sQuery(id+"F0.wireOp",EDGE,"E134"),sQuery(id+"F0.wireOp",EDGE,"E147"),sQuery(id+"F0.wireOp",EDGE,"E272"),sQuery(id+"F0.wireOp",EDGE,"E136"),sQuery(id+"F0.wireOp",EDGE,"E239"),sQuery(id+"F0.wireOp",EDGE,"E144"),sQuery(id+"F0.wireOp",EDGE,"E183"),sQuery(id+"F0.wireOp",EDGE,"E273")])],"isStart":false});
            var Q2;
            Q2=makeQuery(id+"F1.opExtrude","CAP_FACE",FACE,{"disambiguationData":[OSD([sQuery(id+"F0.wireOp",EDGE,"E195"),sQuery(id+"F0.wireOp",EDGE,"E196"),sQuery(id+"F0.wireOp",EDGE,"E200"),sQuery(id+"F0.wireOp",EDGE,"E204"),sQuery(id+"F0.wireOp",EDGE,"E205"),sQuery(id+"F0.wireOp",EDGE,"E206")])],"isStart":false});
            var Q3;
            Q3=makeQuery(id+"F1.opExtrude","CAP_FACE",FACE,{"disambiguationData":[OSD([sQuery(id+"F0.wireOp",EDGE,"E160"),sQuery(id+"F0.wireOp",EDGE,"E164"),sQuery(id+"F0.wireOp",EDGE,"E165"),sQuery(id+"F0.wireOp",EDGE,"E167"),sQuery(id+"F0.wireOp",EDGE,"E168"),sQuery(id+"F0.wireOp",EDGE,"E169")])],"isStart":false});
            var Q4;
            Q4=makeQuery(id+"F1.opExtrude","CAP_FACE",FACE,{"disambiguationData":[OSD([sQuery(id+"F0.wireOp",EDGE,"E122"),sQuery(id+"F0.wireOp",EDGE,"E123"),sQuery(id+"F0.wireOp",EDGE,"E127"),sQuery(id+"F0.wireOp",EDGE,"E131"),sQuery(id+"F0.wireOp",EDGE,"E132"),sQuery(id+"F0.wireOp",EDGE,"E133")])],"isStart":false});
            var Q5;
            Q5=makeQuery(id+"F1.opExtrude","CAP_FACE",FACE,{"disambiguationData":[OSD([sQuery(id+"F0.wireOp",EDGE,"E86"),sQuery(id+"F0.wireOp",EDGE,"E90"),sQuery(id+"F0.wireOp",EDGE,"E91"),sQuery(id+"F0.wireOp",EDGE,"E94"),sQuery(id+"F0.wireOp",EDGE,"E95"),sQuery(id+"F0.wireOp",EDGE,"E96")])],"isStart":false});
            var Q6;
            Q6=makeQuery(id+"F1.opExtrude","CAP_FACE",FACE,{"disambiguationData":[OSD([sQuery(id+"F0.wireOp",EDGE,"E47"),sQuery(id+"F0.wireOp",EDGE,"E48"),sQuery(id+"F0.wireOp",EDGE,"E52"),sQuery(id+"F0.wireOp",EDGE,"E56"),sQuery(id+"F0.wireOp",EDGE,"E57"),sQuery(id+"F0.wireOp",EDGE,"E58")])],"isStart":false});
            extrude(context, id + "F7", {"entities" : qUnion([Q0, Q1, Q2, Q3, Q4, Q5, Q6]), "depth" : 0.5 * mm});
        }
    });
